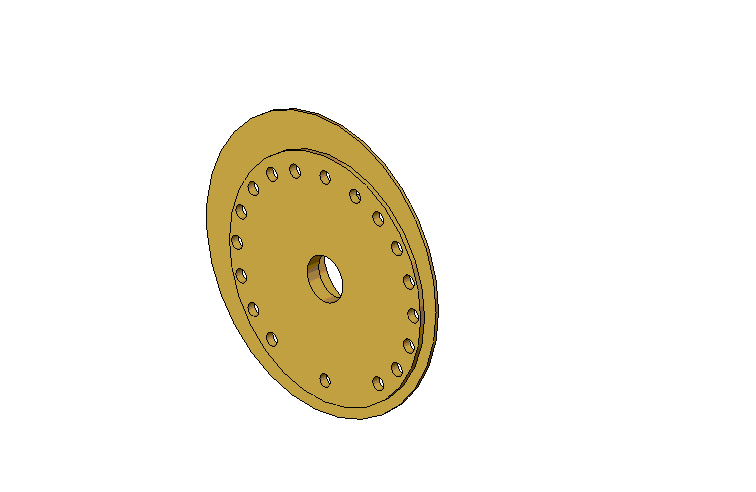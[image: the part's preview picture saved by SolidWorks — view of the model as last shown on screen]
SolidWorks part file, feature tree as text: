
SOLIDWORKS PART (.sldprt)
format: sldprt  version: not decoded by parser v0  size: 297,472 bytes
history: native  units: mm
features: pattern_circular x4, sketch x3, cut_extrude x3, material x1, plane x1 + 1 further entry (+12 scaffold rows collapsed)
feature tree (25):
  scaffold x12  (default folders/planes/origin — collapsed)
  material  "Material <not specified>"
  "4. hinderwand_fin<3>@4. hinderwand_combined"
  plane  "Plane1"  Offset=0mm
  sketch  "Sketch1"  dims[D7=~3.250762mm D1=4.5mm D2=4.5mm D3=31.0mm D4=31.0mm D5=30.0mm D6=30.0mm]
  cut_extrude  "Cut-Extrude2"  [1 undecoded]
  pattern_circular  "CirPattern1"  Count=5 Angle=76deg
  pattern_circular  "CirPattern2"  Count=4 Angle=57deg
  sketch  "Sketch2"  dims[D3=~2.347716mm D1=4.5mm D2=30.0mm]
  cut_extrude  "Cut-Extrude4"  [1 undecoded]
  pattern_circular  "CirPattern3"  Count=5 Angle=76deg
  pattern_circular  "CirPattern4"  Count=4 Angle=57deg
  sketch  "Sketch3"  dims[D3=~1.822335mm D1=31.0mm D2=31.0mm]
  cut_extrude  "Cut-Extrude5"  [1 undecoded]
decode coverage: 7 of 10 modeling features carry decoded parameters; 1 rows unclassified (native names shown)
note: ~ marks probable driven/reference dimensions
note: 3 parameter values undecoded
summary: no parameter record found for 3 features
note: suppression state not decoded; provenance and decode notes live in map.json
